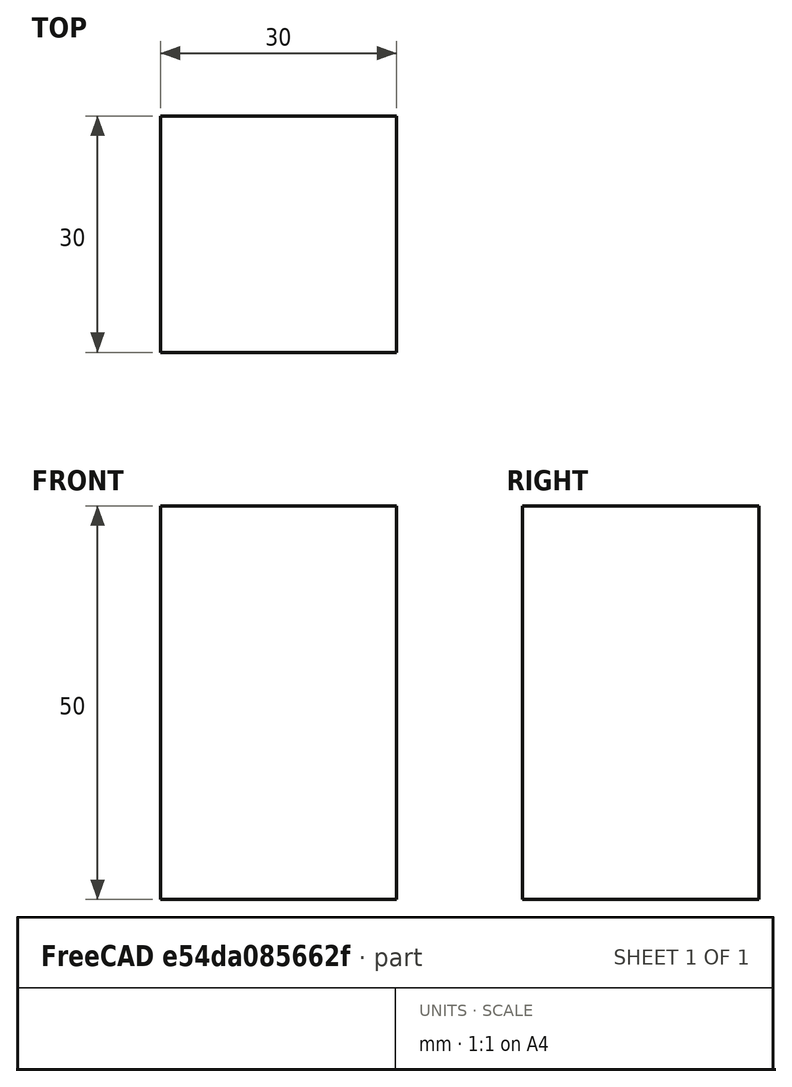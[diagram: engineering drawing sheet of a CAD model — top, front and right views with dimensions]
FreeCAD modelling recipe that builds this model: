
FCSTD DOCUMENT  (FreeCAD 0.15R4671 (Git))
Label: Square Bar 30 EN10059 S235JR
License: All rights reserved
LicenseURL: http://en.wikipedia.org/wiki/All_rights_reserved
objects: Sketcher::SketchObject×1, Part::Extrusion×1
note: 2 computed .brp shape members not serialized (recipe doc carries the construction recipe); baked Part::Feature solids carry a one-line shape summary decoded from their .brp

FEATURE [Sketcher::SketchObject] Sketch
  sketch-geometry (4):
    g0: LineSegment StartX=-15 StartY=-15 StartZ=0 EndX=15 EndY=-15 EndZ=0
    g1: LineSegment StartX=15 StartY=-15 StartZ=0 EndX=15 EndY=15 EndZ=0
    g2: LineSegment StartX=15 StartY=15 StartZ=0 EndX=-15 EndY=15 EndZ=0
    g3: LineSegment StartX=-15 StartY=15 StartZ=0 EndX=-15 EndY=-15 EndZ=0
  constraints (12):
    c: Coincident(g0,g1)
    c: Coincident(g1,g2)
    c: Coincident(g2,g3)
    c: Coincident(g3,g0)
    c: Horizontal(g0)
    c: Horizontal(g2)
    c: Vertical(g1)
    c: Vertical(g3)
    c: Symmetric(g1,g0,g-1)
    c: Symmetric(g2,g1,g-2)
    c: Equal(g1,g2)
    c: DistanceY(g1) = 30
FEATURE [Part::Extrusion] Extrude  label="Square Bar 30 EN10059 S235JR"
  Base = -> Sketch
  Dir = (0,0,50)
  Solid = true
